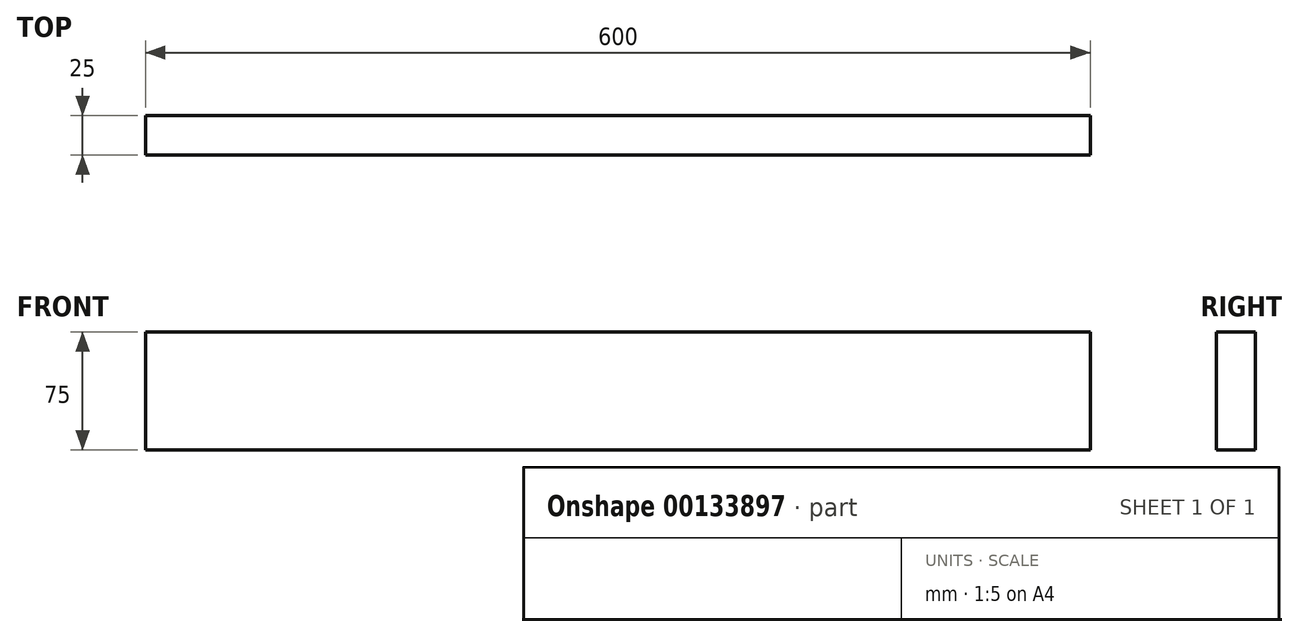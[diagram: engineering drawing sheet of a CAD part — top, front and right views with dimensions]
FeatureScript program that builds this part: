
annotation { "Feature Type Name" : "Feature", "Feature Type Description" : "" }
export const myFeature = defineFeature(function(context is Context, id is Id, definition is map)
    precondition{}
    {
        {
            var Q0;
            Q0=qCreatedBy(makeId("Front.planeOp"),FACE);
            var sketch = newSketch(context, id + "F0", { "sketchPlane" : qUnion([Q0])});
            skLineSegment(sketch, "E0.bottom", {"start": v(300, -26.5) * mm, "end": v(-300, -26.5) * mm});
            skLineSegment(sketch, "E0.top", {"start": v(300, 48.5) * mm, "end": v(-300, 48.5) * mm});
            skLineSegment(sketch, "E0.left", {"start": v(300, -26.5) * mm, "end": v(300, 48.5) * mm});
            skLineSegment(sketch, "E0.right", {"start": v(-300, -26.5) * mm, "end": v(-300, 48.5) * mm});
            skPoint(sketch, "E0.middle", {"position": v(0, 11) * mm});
            skSolve(sketch);
        }
        {
            var Q0;
            Q0=makeQuery(id+"F0.imprint","IMPRINT",FACE,{"disambiguationData":[TD([[makeQuery(id+"F0.imprint","IMPRINT",EDGE,{"derivedFrom":sQuery(id+"F0.wireOp",EDGE,"E0.bottom")}),-1.0]])]});
            extrude(context, id + "F1", {"entities" : qUnion([Q0]), "depth" : 25 * mm});
        }
    });
